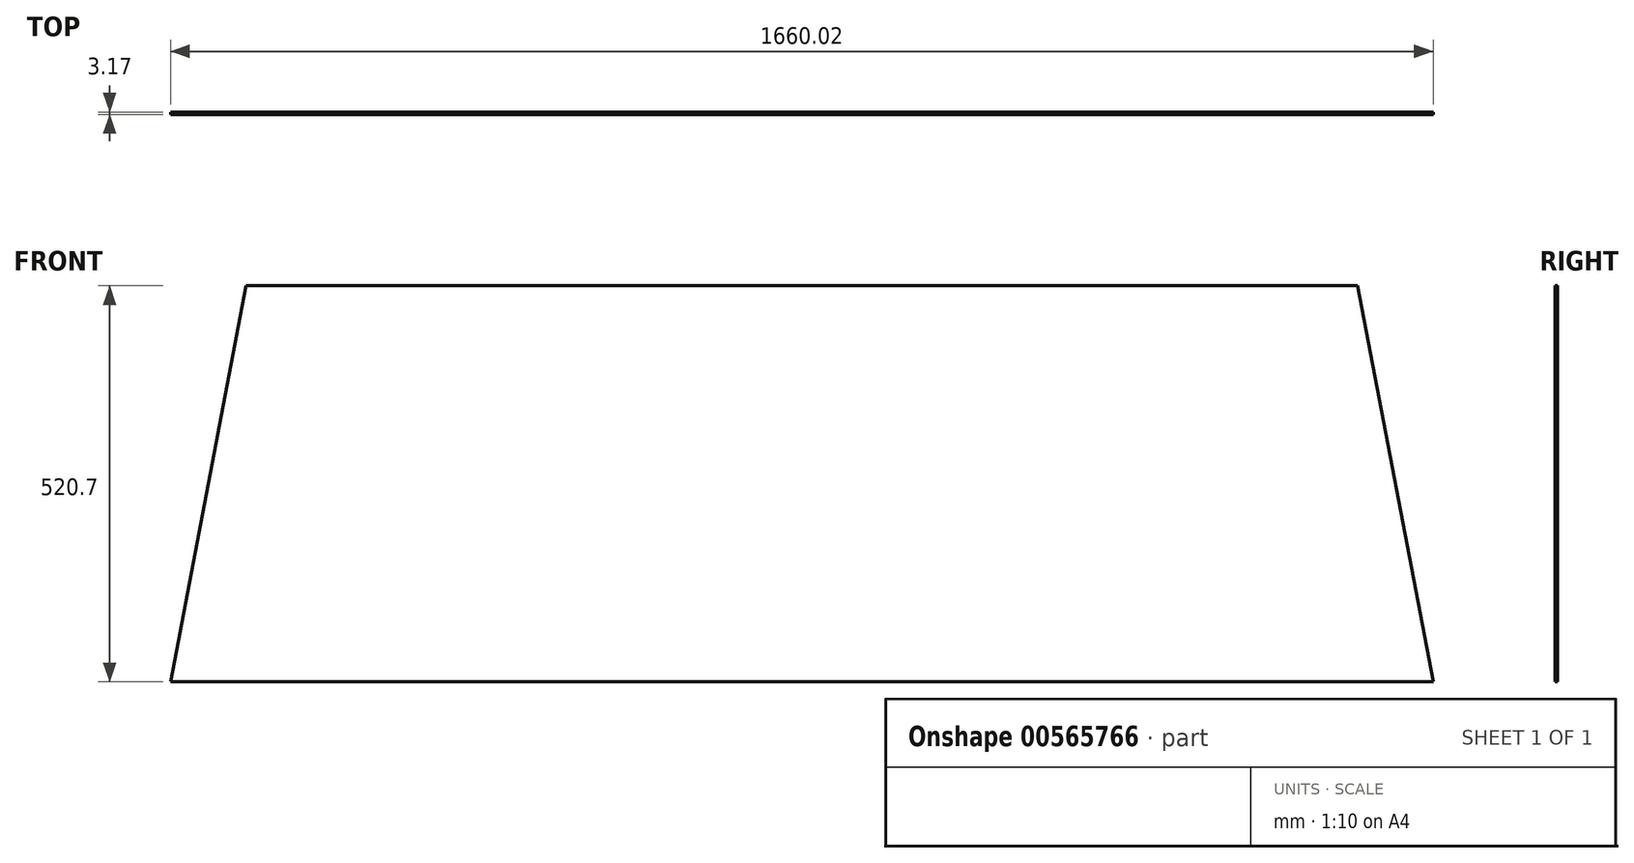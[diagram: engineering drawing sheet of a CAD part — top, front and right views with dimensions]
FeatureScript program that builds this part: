
annotation { "Feature Type Name" : "Feature", "Feature Type Description" : "" }
export const myFeature = defineFeature(function(context is Context, id is Id, definition is map)
    precondition{}
    {
        {
            var Q0;
            Q0=qCreatedBy(makeId("Front.planeOp"),FACE);
            var sketch = newSketch(context, id + "F0", { "sketchPlane" : qUnion([Q0])});
            skLineSegment(sketch, "E0", {"start": v(0, 0) * mm, "end": v(1660.02, 0) * mm});
            skLineSegment(sketch, "E1", {"start": v(1660.02, 0) * mm, "end": v(1560.64, 520.7) * mm});
            skLineSegment(sketch, "E2", {"start": v(1560.64, 520.7) * mm, "end": v(99.38, 520.7) * mm});
            skLineSegment(sketch, "E3", {"start": v(99.38, 520.7) * mm, "end": v(0, 0) * mm});
            skSolve(sketch);
        }
        {
            var Q0;
            Q0=makeQuery(id+"F0.imprint","IMPRINT",FACE,{"disambiguationData":[TD([[makeQuery(id+"F0.imprint","IMPRINT",EDGE,{"derivedFrom":sQuery(id+"F0.wireOp",EDGE,"E0")}),1.0]])]});
            extrude(context, id + "F1", {"entities" : qUnion([Q0]), "depth" : 3.17 * mm, "offsetDistance" : 25.4 * mm});
        }
    });
